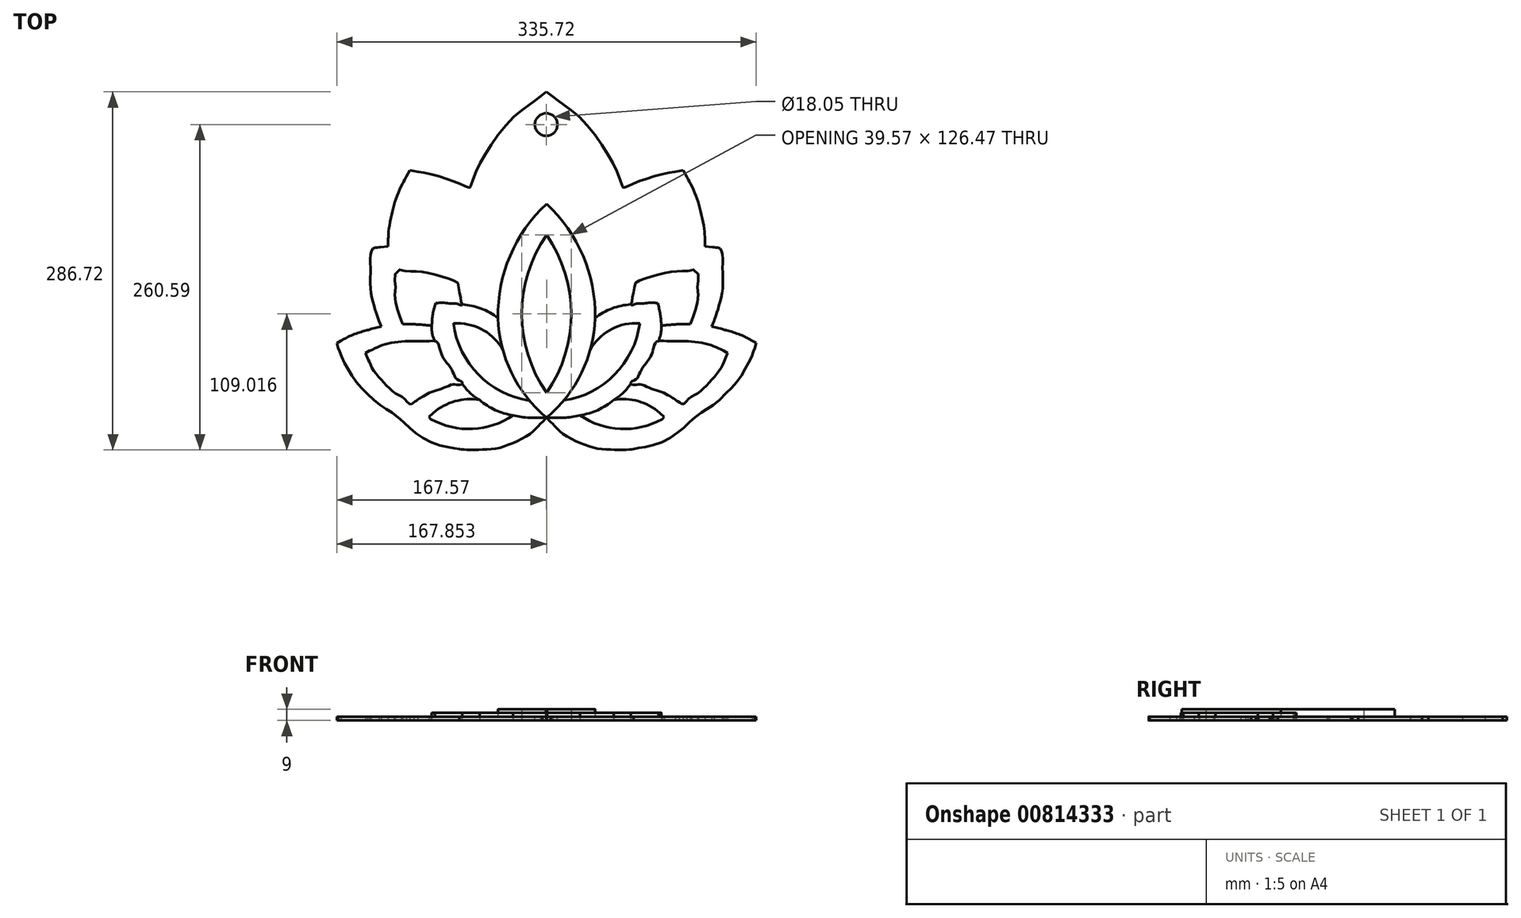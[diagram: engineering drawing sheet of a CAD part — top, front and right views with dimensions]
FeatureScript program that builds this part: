
annotation { "Feature Type Name" : "Feature", "Feature Type Description" : "" }
export const myFeature = defineFeature(function(context is Context, id is Id, definition is map)
    precondition{}
    {
        {
            var Q0;
            Q0=qCreatedBy(makeId("Top.planeOp"),FACE);
            var sketch = newSketch(context, id + "F0", { "sketchPlane" : qUnion([Q0])});
            skLineSegment(sketch, "E0", {"start": v(-166.46, -61.4) * mm, "end": v(-167.57, -57.52) * mm});
            skLineSegment(sketch, "E1", {"start": v(-167.57, -57.52) * mm, "end": v(-164.43, -55.67) * mm});
            skFitSpline(sketch, "E2", {"points": [v(-69.37, -142.53) * mm, v(-74.98, -141.38) * mm, v(-85.87, -139.14) * mm, v(-100.91, -132.02) * mm, v(-110.61, -124.32) * mm, v(-116.75, -118.65) * mm, v(-119.77, -116.1) * mm, v(-125.36, -112.16) * mm, v(-133.98, -106.53) * mm, v(-144.13, -97.12) * mm, v(-152.7, -87.87) * mm, v(-158.7, -78.4) * mm, v(-163.27, -70) * mm, v(-165.47, -64.08) * mm, v(-166.46, -61.4) * mm]});
            skLineSegment(sketch, "E3", {"start": v(-140.09, -46.38) * mm, "end": v(-131.99, -44.34) * mm});
            skLineSegment(sketch, "E4", {"start": v(-131.99, -44.34) * mm, "end": v(-133.82, -39.88) * mm});
            skFitSpline(sketch, "E5", {"points": [v(-164.43, -55.67) * mm, v(-162.17, -54.52) * mm, v(-157.16, -51.96) * mm, v(-148.98, -48.9) * mm, v(-143.05, -47.22) * mm, v(-140.09, -46.38) * mm]});
            skLineSegment(sketch, "E6", {"start": v(-132.52, 19.14) * mm, "end": v(-126.61, 19.66) * mm});
            skLineSegment(sketch, "E7", {"start": v(-126.61, 19.66) * mm, "end": v(-126.61, 24.34) * mm});
            skFitSpline(sketch, "E8", {"points": [v(-133.82, -39.88) * mm, v(-134.25, -38.74) * mm, v(-135.24, -36.06) * mm, v(-136.57, -31.7) * mm, v(-138.87, -23.83) * mm, v(-140.8, -12.2) * mm, v(-140.65, 2.56) * mm, v(-140.56, 12.78) * mm, v(-138.22, 18.44) * mm, v(-135.63, 18.83) * mm, v(-133.77, 19.02) * mm, v(-132.52, 19.14) * mm]});
            skLineSegment(sketch, "E9", {"start": v(-111.9, 75.7) * mm, "end": v(-109.07, 80.64) * mm});
            skLineSegment(sketch, "E10", {"start": v(-109.07, 80.64) * mm, "end": v(-106.08, 80.22) * mm});
            skFitSpline(sketch, "E11", {"points": [v(-126.61, 24.34) * mm, v(-126.41, 27.13) * mm, v(-125.96, 33.5) * mm, v(-124.17, 43.05) * mm, v(-121.99, 52.47) * mm, v(-119, 60.83) * mm, v(-115.79, 68.45) * mm, v(-113.18, 73.3) * mm, v(-111.9, 75.7) * mm]});
            skLineSegment(sketch, "E12", {"start": v(-4.75, 139.96) * mm, "end": v(0.26, 143.5) * mm});
            skFitSpline(sketch, "E13", {"points": [v(-106.08, 80.22) * mm, v(-101.72, 79.43) * mm, v(-92.6, 77.77) * mm, v(-79.35, 73.8) * mm, v(-69.88, 70.35) * mm, v(-64.18, 67.66) * mm, v(-62.58, 67.18) * mm, v(-61.2, 66.42) * mm, v(-60.94, 67.77) * mm, v(-60.24, 69) * mm, v(-56.11, 79.82) * mm, v(-46.25, 97.7) * mm, v(-27.96, 121.55) * mm, v(-12.47, 133.83) * mm, v(-4.75, 139.96) * mm]});
            skLineSegment(sketch, "E14", {"start": v(0.13, -117.21) * mm, "end": v(-0.14, -116.92) * mm});
            skLineSegment(sketch, "E15", {"start": v(0.3, -117.03) * mm, "end": v(-3.15, -120.86) * mm});
            skFitSpline(sketch, "E16", {"points": [v(-3.15, -120.86) * mm, v(-6.47, -124.04) * mm, v(-13.3, -130.58) * mm, v(-26.15, -137.32) * mm, v(-38.35, -141.6) * mm, v(-50.07, -142.76) * mm, v(-59.76, -143.21) * mm, v(-66.43, -142.74) * mm, v(-69.37, -142.53) * mm]});
            skLineSegment(sketch, "E17", {"start": v(-90.36, -113.55) * mm, "end": v(-93.85, -116.63) * mm});
            skLineSegment(sketch, "E18", {"start": v(-93.85, -116.63) * mm, "end": v(-92.14, -118.5) * mm});
            skLineSegment(sketch, "E19", {"start": v(-141.38, -63.74) * mm, "end": v(-144.52, -65.67) * mm});
            skLineSegment(sketch, "E20", {"start": v(-144.52, -65.67) * mm, "end": v(-143.08, -69.46) * mm});
            skFitSpline(sketch, "E21", {"points": [v(-103.03, -102.99) * mm, v(-99.77, -101.08) * mm, v(-93.06, -97.16) * mm, v(-82.13, -93.53) * mm, v(-73.96, -90.65) * mm, v(-68.61, -91.06) * mm, v(-67.09, -89.2) * mm, v(-71.68, -86.36) * mm, v(-74.92, -80.17) * mm, v(-81.34, -70.98) * mm, v(-84.92, -63.23) * mm, v(-87.59, -56.62) * mm, v(-95.33, -56.06) * mm, v(-105.15, -56.04) * mm, v(-118.08, -56.57) * mm, v(-130.65, -58.97) * mm, v(-138, -62.24) * mm, v(-141.58, -63.82) * mm]});
            skFitSpline(sketch, "E22", {"points": [v(-143.08, -69.46) * mm, v(-141.88, -72.04) * mm, v(-139.44, -77.32) * mm, v(-134.09, -84.68) * mm, v(-127.65, -91.57) * mm, v(-120.17, -98.19) * mm, v(-113.72, -101.93) * mm, v(-108.9, -106.62) * mm, v(-106.21, -105.07) * mm, v(-104.27, -103.88) * mm, v(-102.66, -102.79) * mm, v(-101.74, -102.17) * mm]});
            skLineSegment(sketch, "E23", {"start": v(-71.01, -41.76) * mm, "end": v(-74.35, -41.76) * mm});
            skLineSegment(sketch, "E24", {"start": v(-116.05, -39.22) * mm, "end": v(-114.9, -42.4) * mm});
            skLineSegment(sketch, "E25", {"start": v(-114.9, -42.4) * mm, "end": v(-108.1, -42.48) * mm});
            skFitSpline(sketch, "E26", {"points": [v(-88.6, -25.55) * mm, v(-86.89, -25.46) * mm, v(-82.74, -25.22) * mm, v(-76.58, -25.86) * mm, v(-71.3, -26.1) * mm, v(-68.6, -27.23) * mm, v(-67.15, -26.83) * mm, v(-67.82, -25.37) * mm, v(-68.04, -23.5) * mm, v(-68.72, -20.43) * mm, v(-69.44, -16.34) * mm, v(-70.01, -12.53) * mm, v(-71.1, -9.16) * mm, v(-74.72, -7.29) * mm, v(-80.49, -5.25) * mm, v(-88.62, -2.9) * mm, v(-96, -1.1) * mm, v(-102.08, -0.36) * mm, v(-106.88, 0.1) * mm, v(-112.1, -0.05) * mm, v(-117.43, 1.18) * mm, v(-121.41, -3.7) * mm, v(-120.52, -10.78) * mm, v(-121.16, -19.5) * mm, v(-119.33, -29.37) * mm, v(-117.18, -35.82) * mm, v(-116.05, -39.22) * mm]});
            skLineSegment(sketch, "E27", {"start": v(-34.8, -8.07) * mm, "end": v(-34.8, -8.07) * mm});
            skArc(sketch, "E28", {"start": v(-38.58, -37.54) * mm, "mid": v(-27.8, -81.32) * mm, "end": v(-0.14, -116.92) * mm});
            skArc(sketch, "E29", {"start": v(-38.58, -37.54) * mm, "mid": v(-52.15, -29.87) * mm, "end": v(-67.4, -26.66) * mm});
            skPoint(sketch, "E30.endSnap0", {"position": v(-52.15, -29.87) * mm});
            skArc(sketch, "E31", {"start": v(-0.14, -116.92) * mm, "mid": v(0.08, -116.8) * mm, "end": v(0.3, -116.66) * mm});
            skLineSegment(sketch, "E32", {"start": v(0.26, 143.5) * mm, "end": v(0.3, -117.03) * mm});
            skPoint(sketch, "E33.center.orphan", {"position": v(0, 124.39) * mm});
            skArc(sketch, "E34", {"start": v(-92.14, -118.5) * mm, "mid": v(-58.86, -126.34) * mm, "end": v(-26.46, -115.44) * mm});
            skArc(sketch, "E35", {"start": v(-53.38, -103.18) * mm, "mid": v(-73.05, -104.15) * mm, "end": v(-90.36, -113.55) * mm});
            skArc(sketch, "E36", {"start": v(-53.38, -103.18) * mm, "mid": v(-40.79, -111.22) * mm, "end": v(-26.46, -115.44) * mm});
            skArc(sketch, "E37", {"start": v(-26.46, -115.44) * mm, "mid": v(-13.15, -117.36) * mm, "end": v(0.3, -117.03) * mm});
            skArc(sketch, "E38", {"start": v(-67.7, -89.03) * mm, "mid": v(-61.46, -97.04) * mm, "end": v(-53.38, -103.18) * mm});
            skArc(sketch, "E39", {"start": v(-91.56, -43.75) * mm, "mid": v(-91.09, -50.57) * mm, "end": v(-88.72, -56.99) * mm});
            skArc(sketch, "E40", {"start": v(-74.35, -41.76) * mm, "mid": v(-54.22, -82.82) * mm, "end": v(-13.45, -103.53) * mm});
            skArc(sketch, "E41", {"start": v(-34.69, -63.04) * mm, "mid": v(-49.96, -47.47) * mm, "end": v(-71.01, -41.76) * mm});
            skArc(sketch, "E42", {"start": v(-88.6, -25.55) * mm, "mid": v(-90.75, -34.54) * mm, "end": v(-91.56, -43.75) * mm});
            skArc(sketch, "E43", {"start": v(-91.56, -43.75) * mm, "mid": v(-99.8, -42.85) * mm, "end": v(-108.1, -42.48) * mm});
            skArc(sketch, "E44", {"start": v(0.27, 29.03) * mm, "mid": v(-19.5, -34.2) * mm, "end": v(0.3, -97.44) * mm});
            skArc(sketch, "E45", {"start": v(0.27, 53.73) * mm, "mid": v(-28.94, 12.26) * mm, "end": v(-38.58, -37.54) * mm});
            skSolve(sketch);
        }
        {
            var Q0;
            {var subQ0=sQuery(id+"F0.wireOp",EDGE,"E31");Q0=makeQuery(id+"F0.imprint","IMPRINT",FACE,{"disambiguationData":[TD([[makeQuery(id+"F0.imprint","IMPRINT",EDGE,{"derivedFrom":subQ0}),1.0]])]});}
            var Q1;
            Q1=makeQuery(id+"F0.imprint","IMPRINT",FACE,{"disambiguationData":[TD([[makeQuery(id+"F0.imprint","IMPRINT",EDGE,{"derivedFrom":sQuery(id+"F0.wireOp",EDGE,"E0")}),-1.0]])]});
            var Q2;
            Q2=makeQuery(id+"F0.imprint","IMPRINT",FACE,{"disambiguationData":[TD([[makeQuery(id+"F0.imprint","IMPRINT",EDGE,{"derivedFrom":sQuery(id+"F0.wireOp",EDGE,"E23")}),-1.0]])]});
            extrude(context, id + "F1", {"entities" : qUnion([Q0, Q1, Q2]), "depth" : 3 * mm, "offsetDistance" : 25 * mm});
        }
        {
            var Q0;
            {var subQ0=sQuery(id+"F0.wireOp",EDGE,"E31");Q0=makeQuery(id+"F0.imprint","IMPRINT",FACE,{"disambiguationData":[TD([[makeQuery(id+"F0.imprint","IMPRINT",EDGE,{"derivedFrom":subQ0}),1.0]])]});}
            extrude(context, id + "F2", {"entities" : qUnion([Q0]), "depth" : 9 * mm, "offsetDistance" : 25 * mm});
        }
        {
            var Q0;
            Q0=makeQuery(id+"F0.imprint","IMPRINT",FACE,{"disambiguationData":[TD([[makeQuery(id+"F0.imprint","IMPRINT",EDGE,{"derivedFrom":sQuery(id+"F0.wireOp",EDGE,"E23")}),-1.0]])]});
            extrude(context, id + "F3", {"entities" : qUnion([Q0]), "operationType" : NewBodyOperationType.ADD, "depth" : 6 * mm, "offsetDistance" : 25 * mm});
        }
        {
            var Q0;
            Q0=makeQuery(id+"F1.opExtrude","SWEPT_BODY",BODY,{"disambiguationData":[OSD([sQuery(id+"F0.wireOp",EDGE,"E0"),sQuery(id+"F0.wireOp",EDGE,"E1"),sQuery(id+"F0.wireOp",EDGE,"E2"),sQuery(id+"F0.wireOp",EDGE,"E3"),sQuery(id+"F0.wireOp",EDGE,"E4"),sQuery(id+"F0.wireOp",EDGE,"E5"),sQuery(id+"F0.wireOp",EDGE,"E6"),sQuery(id+"F0.wireOp",EDGE,"E7"),sQuery(id+"F0.wireOp",EDGE,"E8"),sQuery(id+"F0.wireOp",EDGE,"E9"),sQuery(id+"F0.wireOp",EDGE,"E10"),sQuery(id+"F0.wireOp",EDGE,"E11"),sQuery(id+"F0.wireOp",EDGE,"E12"),sQuery(id+"F0.wireOp",EDGE,"E13"),sQuery(id+"F0.wireOp",EDGE,"E14"),sQuery(id+"F0.wireOp",EDGE,"E15"),sQuery(id+"F0.wireOp",EDGE,"E16"),sQuery(id+"F0.wireOp",EDGE,"E17"),sQuery(id+"F0.wireOp",EDGE,"E18"),sQuery(id+"F0.wireOp",EDGE,"E19"),sQuery(id+"F0.wireOp",EDGE,"E20"),sQuery(id+"F0.wireOp",EDGE,"E21"),sQuery(id+"F0.wireOp",EDGE,"E22"),sQuery(id+"F0.wireOp",EDGE,"E23"),sQuery(id+"F0.wireOp",EDGE,"E24"),sQuery(id+"F0.wireOp",EDGE,"E25"),sQuery(id+"F0.wireOp",EDGE,"E26"),sQuery(id+"F0.wireOp",EDGE,"E28"),sQuery(id+"F0.wireOp",EDGE,"E31"),sQuery(id+"F0.wireOp",EDGE,"E32"),sQuery(id+"F0.wireOp",EDGE,"E34"),sQuery(id+"F0.wireOp",EDGE,"E35"),sQuery(id+"F0.wireOp",EDGE,"E36"),sQuery(id+"F0.wireOp",EDGE,"E40"),sQuery(id+"F0.wireOp",EDGE,"E41"),sQuery(id+"F0.wireOp",EDGE,"E42"),sQuery(id+"F0.wireOp",EDGE,"E43"),sQuery(id+"F0.wireOp",EDGE,"E44")])]});
            var Q1;
            Q1=makeQuery(id+"F3.opExtrude","SWEPT_BODY",BODY,{"disambiguationData":[OSD([sQuery(id+"F0.wireOp",EDGE,"E14"),sQuery(id+"F0.wireOp",EDGE,"E21"),sQuery(id+"F0.wireOp",EDGE,"E23"),sQuery(id+"F0.wireOp",EDGE,"E26"),sQuery(id+"F0.wireOp",EDGE,"E28"),sQuery(id+"F0.wireOp",EDGE,"E29"),sQuery(id+"F0.wireOp",EDGE,"E36"),sQuery(id+"F0.wireOp",EDGE,"E37"),sQuery(id+"F0.wireOp",EDGE,"E38"),sQuery(id+"F0.wireOp",EDGE,"E39"),sQuery(id+"F0.wireOp",EDGE,"E40"),sQuery(id+"F0.wireOp",EDGE,"E41"),sQuery(id+"F0.wireOp",EDGE,"E42")])]});
            var Q2;
            Q2=makeQuery(id+"F2.opExtrude","SWEPT_BODY",BODY,{"disambiguationData":[OSD([sQuery(id+"F0.wireOp",EDGE,"E28"),sQuery(id+"F0.wireOp",EDGE,"E31"),sQuery(id+"F0.wireOp",EDGE,"E32"),sQuery(id+"F0.wireOp",EDGE,"E44"),sQuery(id+"F0.wireOp",EDGE,"E45")])]});
            var Q3;
            {var subQ0=sQuery(id+"F0.wireOp",EDGE,"E32");Q3=makeQuery(id+"F1.opExtrude","SWEPT_FACE",FACE,{"disambiguationData":[OSD([subQ0]),TDD([makeQuery(id+"F0.imprint","IMPRINT",EDGE,{"disambiguationData":[TD([[makeQuery(id+"F0.imprint","INTERSECT",VERTEX,{"derivedFrom":[sQuery(id+"F0.wireOp",EDGE,"E12"),subQ0]}),-1.0]])],"derivedFrom":subQ0}),makeQuery(id+"F0.imprint","IMPRINT",EDGE,{"disambiguationData":[TD([[makeQuery(id+"F0.imprint","INTERSECT",VERTEX,{"disambiguationData":[OD(0.0)],"derivedFrom":[subQ0,sQuery(id+"F0.wireOp",EDGE,"E44")]}),1.0]])],"derivedFrom":subQ0})])]});}
            mirror(context, id + "F4", {"operationType" : NewBodyOperationType.ADD, "entities" : qUnion([Q0, Q1, Q2]), "mirrorPlane" : qUnion([Q3])});
        }
        {
            var Q0;
            {var subQ0=makeQuery(id+"F1.opExtrude","CAP_FACE",FACE,{"disambiguationData":[OSD([sQuery(id+"F0.wireOp",EDGE,"E0"),sQuery(id+"F0.wireOp",EDGE,"E1"),sQuery(id+"F0.wireOp",EDGE,"E2"),sQuery(id+"F0.wireOp",EDGE,"E3"),sQuery(id+"F0.wireOp",EDGE,"E4"),sQuery(id+"F0.wireOp",EDGE,"E5"),sQuery(id+"F0.wireOp",EDGE,"E6"),sQuery(id+"F0.wireOp",EDGE,"E7"),sQuery(id+"F0.wireOp",EDGE,"E8"),sQuery(id+"F0.wireOp",EDGE,"E9"),sQuery(id+"F0.wireOp",EDGE,"E10"),sQuery(id+"F0.wireOp",EDGE,"E11"),sQuery(id+"F0.wireOp",EDGE,"E12"),sQuery(id+"F0.wireOp",EDGE,"E13"),sQuery(id+"F0.wireOp",EDGE,"E14"),sQuery(id+"F0.wireOp",EDGE,"E15"),sQuery(id+"F0.wireOp",EDGE,"E16"),sQuery(id+"F0.wireOp",EDGE,"E17"),sQuery(id+"F0.wireOp",EDGE,"E18"),sQuery(id+"F0.wireOp",EDGE,"E19"),sQuery(id+"F0.wireOp",EDGE,"E20"),sQuery(id+"F0.wireOp",EDGE,"E21"),sQuery(id+"F0.wireOp",EDGE,"E22"),sQuery(id+"F0.wireOp",EDGE,"E23"),sQuery(id+"F0.wireOp",EDGE,"E24"),sQuery(id+"F0.wireOp",EDGE,"E25"),sQuery(id+"F0.wireOp",EDGE,"E26"),sQuery(id+"F0.wireOp",EDGE,"E28"),sQuery(id+"F0.wireOp",EDGE,"E31"),sQuery(id+"F0.wireOp",EDGE,"E32"),sQuery(id+"F0.wireOp",EDGE,"E34"),sQuery(id+"F0.wireOp",EDGE,"E35"),sQuery(id+"F0.wireOp",EDGE,"E36"),sQuery(id+"F0.wireOp",EDGE,"E40"),sQuery(id+"F0.wireOp",EDGE,"E41"),sQuery(id+"F0.wireOp",EDGE,"E42"),sQuery(id+"F0.wireOp",EDGE,"E43"),sQuery(id+"F0.wireOp",EDGE,"E44")])],"isStart":false});Q0=makeQuery(id+"F4.boolean.opBoolean","MERGE",FACE,{"derivedFrom":[subQ0,makeQuery(id+"F4.opPattern","COPY",FACE,{"derivedFrom":subQ0,"instanceName":"1"})]});}
            var sketch = newSketch(context, id + "F5", { "sketchPlane" : qUnion([Q0])});
            skCircle(sketch, "E46", {"center": v(0, 117.37) * mm, "radius": 9.03 * mm});
            skSolve(sketch);
        }
        {
            var Q0;
            Q0=makeQuery(id+"F5.imprint","IMPRINT",FACE,{"disambiguationData":[TD([[makeQuery(id+"F5.imprint","IMPRINT",EDGE,{"derivedFrom":sQuery(id+"F5.wireOp",EDGE,"E46")}),1.0]])]});
            extrude(context, id + "F6", {"entities" : qUnion([Q0]), "operationType" : NewBodyOperationType.REMOVE, "oppositeDirection" : true, "depth" : 25 * mm, "offsetDistance" : 25 * mm});
        }
    });
